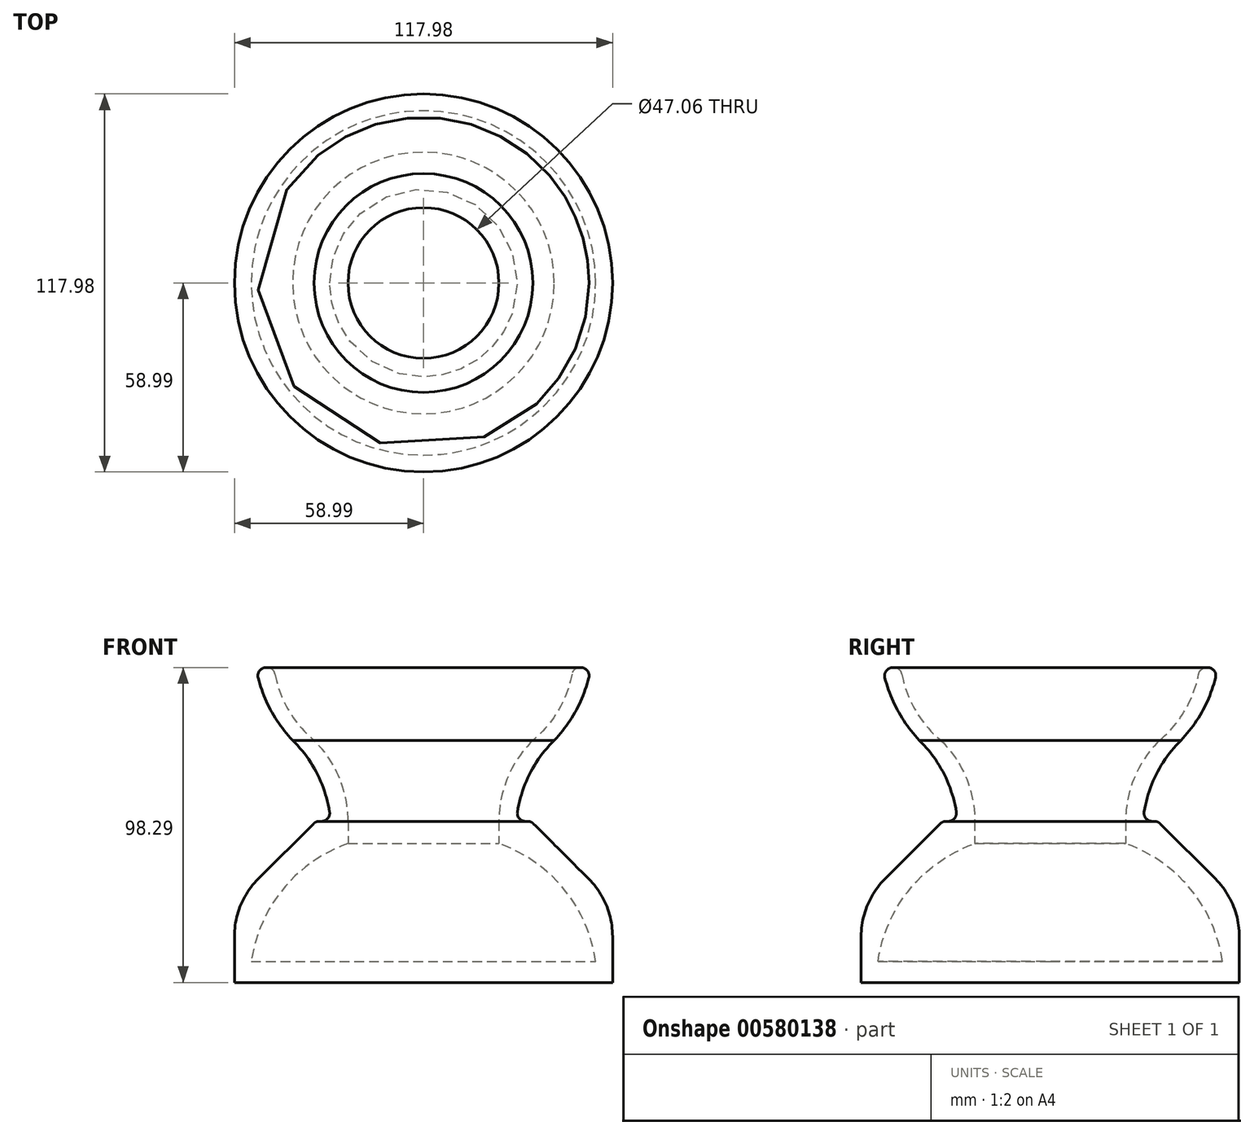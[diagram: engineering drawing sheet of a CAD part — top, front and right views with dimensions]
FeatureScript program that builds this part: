
annotation { "Feature Type Name" : "Feature", "Feature Type Description" : "" }
export const myFeature = defineFeature(function(context is Context, id is Id, definition is map)
    precondition{}
    {
        {
            var Q0;
            Q0=qCreatedBy(makeId("Front.planeOp"),FACE);
            var sketch = newSketch(context, id + "F0", { "sketchPlane" : qUnion([Q0])});
            skLineSegment(sketch, "E0.bottom", {"start": v(0, 0) * mm, "end": v(-59, 0) * mm});
            skLineSegment(sketch, "E0.top", {"start": v(0, 6.58) * mm, "end": v(-53.74, 6.58) * mm});
            skLineSegment(sketch, "E0.left", {"start": v(0, 0) * mm, "end": v(0, 6.58) * mm});
            skLineSegment(sketch, "E0.right", {"start": v(-59, 0) * mm, "end": v(-59, 6.58) * mm});
            skLineSegment(sketch, "E1.bottom", {"start": v(-59, 0) * mm, "end": v(-54.22, 0) * mm});
            skLineSegment(sketch, "E1.left", {"start": v(-59, 0) * mm, "end": v(-59, 43.36) * mm});
            skLineSegment(sketch, "E2.top", {"start": v(-59, 50.28) * mm, "end": v(-23.53, 50.28) * mm});
            skLineSegment(sketch, "E2.left", {"start": v(-59, 43.36) * mm, "end": v(-59, 50.28) * mm});
            skLineSegment(sketch, "E2.right", {"start": v(-23.53, 43.36) * mm, "end": v(-23.53, 50.28) * mm});
            skArc(sketch, "E3", {"start": v(-23.53, 43.36) * mm, "mid": v(-43.77, 29.18) * mm, "end": v(-53.74, 6.58) * mm});
            skArc(sketch, "E4", {"start": v(-23.53, 50.28) * mm, "mid": v(-26.3, 64) * mm, "end": v(-34.14, 75.57) * mm});
            skArc(sketch, "E5", {"start": v(-28.94, 50.28) * mm, "mid": v(-32.61, 64) * mm, "end": v(-40.83, 75.57) * mm});
            skArc(sketch, "E6", {"start": v(-52.27, 98.29) * mm, "mid": v(-48.22, 86.09) * mm, "end": v(-40.83, 75.57) * mm});
            skArc(sketch, "E7", {"start": v(-46.63, 98.29) * mm, "mid": v(-42.53, 85.75) * mm, "end": v(-34.14, 75.57) * mm});
            skLineSegment(sketch, "E8", {"start": v(-52.27, 98.29) * mm, "end": v(-46.63, 98.29) * mm});
            skSolve(sketch);
        }
        {
            var Q0;
            Q0 = qSketchRegion(id + "F0", true);
            var Q1;
            Q1=sQuery(id+"F0.wireOp",EDGE,"E0.left");
            revolve(context, id + "F1", {"entities" : qUnion([Q0]), "axis" : qUnion([Q1]), "revolveType" : RevolveType.FULL});
        }
        {
            var Q0;
            Q0=makeQuery(id+"F1.opRevolve","SWEPT_EDGE",EDGE,{"disambiguationData":[OSD([sQuery(id+"F0.wireOp",EDGE,"E2.top"),sQuery(id+"F0.wireOp",EDGE,"E2.left")])]});
            chamfer(context, id + "F2", {"entities" : qUnion([Q0]), "width" : 25.4 * mm, "tangentPropagation" : true});
        }
        {
            var Q0;
            {var subQ0=sQuery(id+"F0.wireOp",EDGE,"E2.top");Q0=makeQuery(id+"F2.opChamfer","BLEND_EDGE",EDGE,{"blendedFrom":[makeQuery(id+"F1.opRevolve","SWEPT_EDGE",EDGE,{"disambiguationData":[OSD([subQ0,sQuery(id+"F0.wireOp",EDGE,"E2.left")])]}),makeQuery(id+"F1.opRevolve","SWEPT_FACE",FACE,{"disambiguationData":[OSD([subQ0])]})],"blendedInto":[makeQuery(id+"F1.opRevolve","SWEPT_FACE",FACE,{"disambiguationData":[OSD([subQ0])]})]});}
            var Q1;
            Q1=makeQuery(id+"F1.opRevolve","SWEPT_EDGE",EDGE,{"disambiguationData":[OSD([sQuery(id+"F0.wireOp",EDGE,"E2.top"),sQuery(id+"F0.wireOp",EDGE,"E5")])]});
            fillet(context, id + "F3", {"entities" : qUnion([Q0, Q1]), "radius" : 2.54 * mm, "tangentPropagation" : true, "allowEdgeOverflow" : false});
        }
        {
            var Q0;
            Q0=makeQuery(id+"F1.opRevolve","SWEPT_EDGE",EDGE,{"disambiguationData":[OSD([sQuery(id+"F0.wireOp",EDGE,"E7"),sQuery(id+"F0.wireOp",EDGE,"E8")])]});
            var Q1;
            Q1=makeQuery(id+"F1.opRevolve","SWEPT_EDGE",EDGE,{"disambiguationData":[OSD([sQuery(id+"F0.wireOp",EDGE,"E6"),sQuery(id+"F0.wireOp",EDGE,"E8")])]});
            fillet(context, id + "F4", {"entities" : qUnion([Q0, Q1]), "radius" : 2.54 * mm, "tangentPropagation" : true, "allowEdgeOverflow" : false});
        }
        {
            var Q0;
            {var subQ0=sQuery(id+"F0.wireOp",EDGE,"E2.left");Q0=makeQuery(id+"F2.opChamfer","BLEND_EDGE",EDGE,{"blendedFrom":[makeQuery(id+"F1.opRevolve","SWEPT_EDGE",EDGE,{"disambiguationData":[OSD([sQuery(id+"F0.wireOp",EDGE,"E2.top"),subQ0])]}),makeQuery(id+"F1.opRevolve","SWEPT_FACE",FACE,{"disambiguationData":[OSD([sQuery(id+"F0.wireOp",EDGE,"E1.left"),subQ0])]})],"blendedInto":[makeQuery(id+"F1.opRevolve","SWEPT_FACE",FACE,{"disambiguationData":[OSD([sQuery(id+"F0.wireOp",EDGE,"E1.left"),subQ0])]})]});}
            fillet(context, id + "F5", {"entities" : qUnion([Q0]), "radius" : 25.4 * mm, "tangentPropagation" : true, "allowEdgeOverflow" : false});
        }
    });
